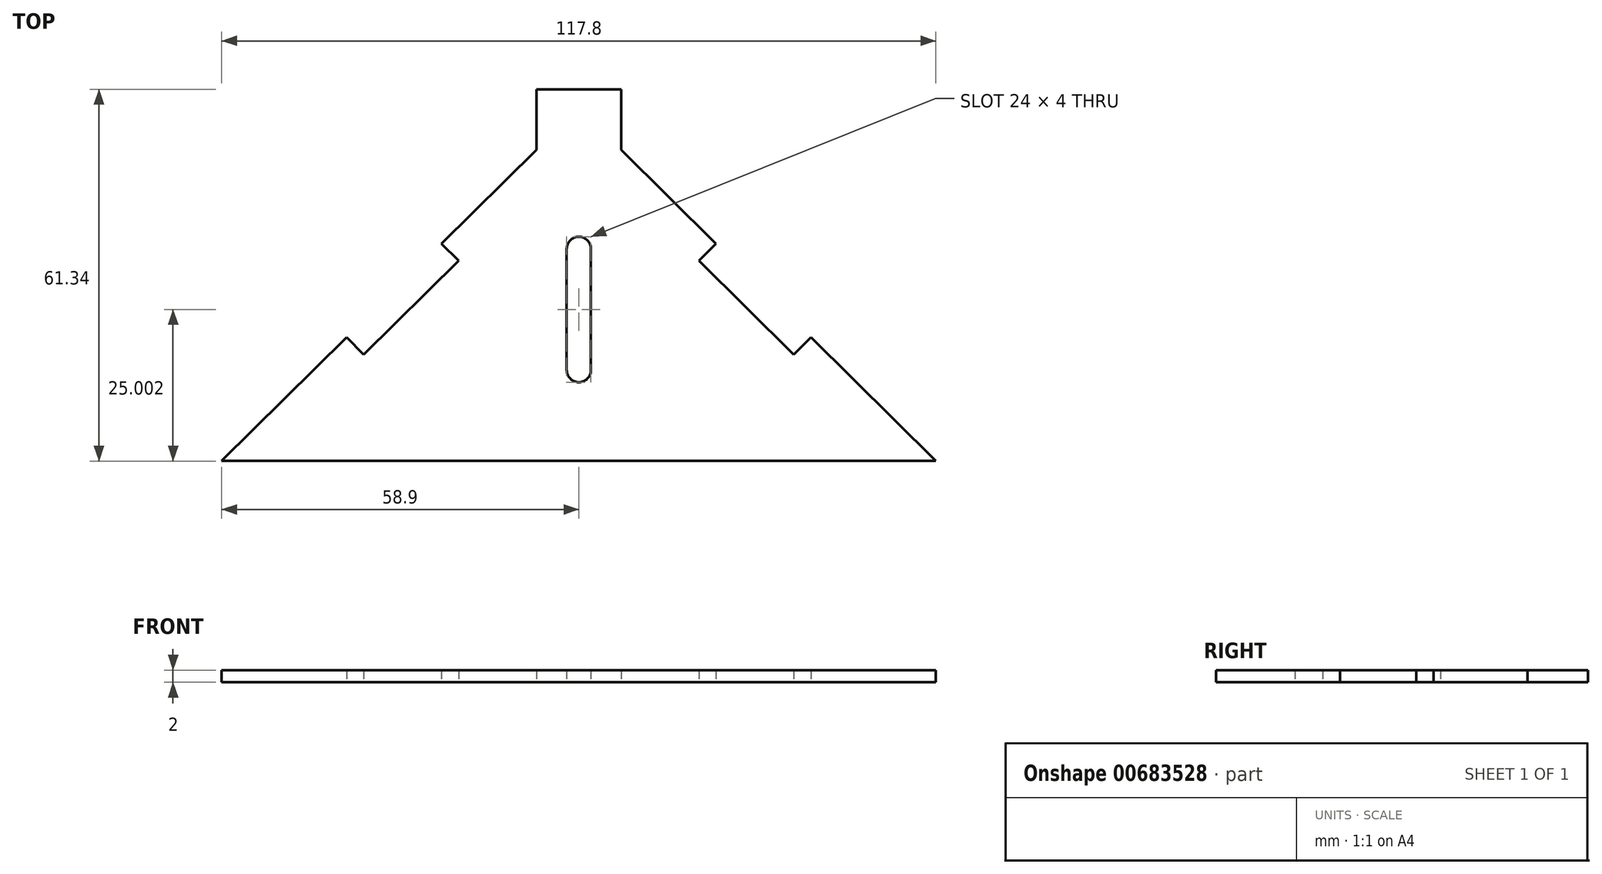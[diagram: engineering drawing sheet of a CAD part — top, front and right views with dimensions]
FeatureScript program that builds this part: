
annotation { "Feature Type Name" : "Feature", "Feature Type Description" : "" }
export const myFeature = defineFeature(function(context is Context, id is Id, definition is map)
    precondition{}
    {
        {
            var Q0;
            Q0=qCreatedBy(makeId("Top.planeOp"),FACE);
            var sketch = newSketch(context, id + "F0", { "sketchPlane" : qUnion([Q0])});
            skLineSegment(sketch, "E0", {"start": v(-21.83, 25.05) * mm, "end": v(-24.64, 27.89) * mm});
            skLineSegment(sketch, "E1", {"start": v(-9, 43.36) * mm, "end": v(-9, 53.36) * mm});
            skLineSegment(sketch, "E2", {"start": v(-9, 53.36) * mm, "end": v(5, 53.36) * mm});
            skLineSegment(sketch, "E3", {"start": v(5, 53.36) * mm, "end": v(5, 43.36) * mm});
            skLineSegment(sketch, "E4", {"start": v(-21.83, 25.05) * mm, "end": v(-37.47, 9.57) * mm});
            skLineSegment(sketch, "E5", {"start": v(-37.47, 9.57) * mm, "end": v(-40.28, 12.42) * mm});
            skLineSegment(sketch, "E6", {"start": v(-9, 43.36) * mm, "end": v(-24.64, 27.89) * mm});
            skLineSegment(sketch, "E7", {"start": v(-40.28, 12.42) * mm, "end": v(-60.9, -7.98) * mm});
            skLineSegment(sketch, "E8", {"start": v(17.83, 25.05) * mm, "end": v(20.64, 27.89) * mm});
            skLineSegment(sketch, "E9", {"start": v(20.64, 27.89) * mm, "end": v(17.83, 25.05) * mm});
            skLineSegment(sketch, "E10", {"start": v(17.83, 25.05) * mm, "end": v(33.47, 9.57) * mm});
            skLineSegment(sketch, "E11", {"start": v(33.47, 9.57) * mm, "end": v(36.28, 12.42) * mm});
            skLineSegment(sketch, "E12", {"start": v(5, 43.36) * mm, "end": v(20.64, 27.89) * mm});
            skLineSegment(sketch, "E13", {"start": v(36.28, 12.42) * mm, "end": v(56.9, -7.98) * mm});
            skLineSegment(sketch, "E14", {"start": v(-60.9, -7.98) * mm, "end": v(56.9, -7.98) * mm});
            skLineSegment(sketch, "E15", {"start": v(0, 7.02) * mm, "end": v(0, 27.02) * mm});
            skLineSegment(sketch, "E16", {"start": v(-4, 27.02) * mm, "end": v(-4, 7.02) * mm});
            skArc(sketch, "E17", {"start": v(0, 27.02) * mm, "mid": v(-2, 29.02) * mm, "end": v(-4, 27.02) * mm});
            skArc(sketch, "E18", {"start": v(-4, 7.02) * mm, "mid": v(-2, 5.02) * mm, "end": v(0, 7.02) * mm});
            skSolve(sketch);
        }
        {
            var Q0;
            Q0 = qSketchRegion(id + "F0", true);
            extrude(context, id + "F1", {"entities" : qUnion([Q0]), "depth" : 2 * mm, "offsetDistance" : 25 * mm});
        }
    });
